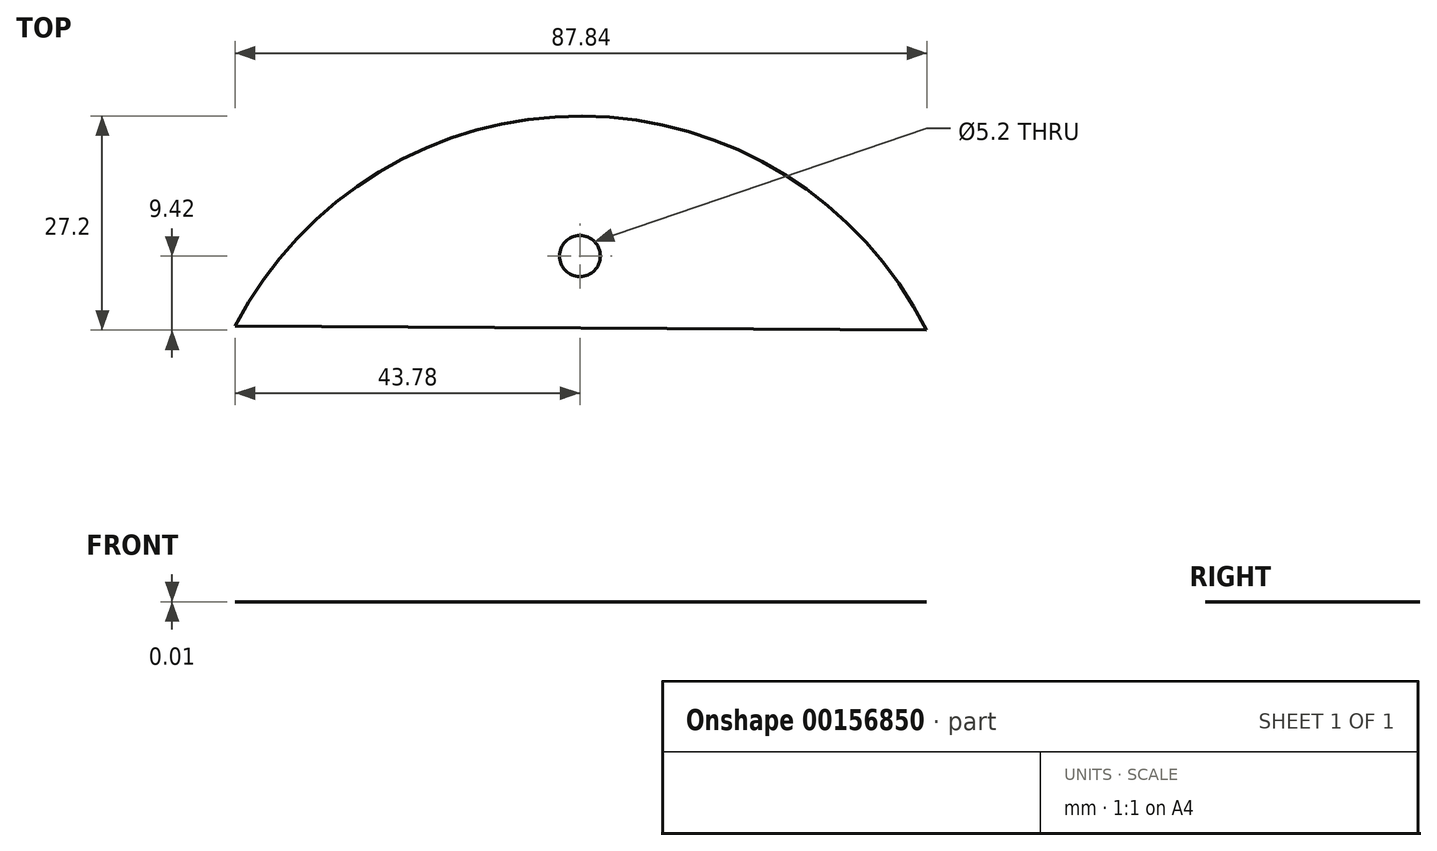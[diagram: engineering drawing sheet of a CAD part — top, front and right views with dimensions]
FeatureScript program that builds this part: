
annotation { "Feature Type Name" : "Feature", "Feature Type Description" : "" }
export const myFeature = defineFeature(function(context is Context, id is Id, definition is map)
    precondition{}
    {
        {
            var Q0;
            Q0=qCreatedBy(makeId("Top.planeOp"),FACE);
            var sketch = newSketch(context, id + "F0", { "sketchPlane" : qUnion([Q0])});
            skPoint(sketch, "E0.center.orphan", {"position": v(0, 0) * mm});
            skPoint(sketch, "E0.end.orphan", {"position": v(43.38, -20.08) * mm});
            skPoint(sketch, "E0.start.orphan", {"position": v(-43.12, -20.62) * mm});
            skArc(sketch, "E1", {"start": v(44.06, 22.08) * mm, "mid": v(0.3, 49.28) * mm, "end": v(-43.78, 22.62) * mm});
            skPoint(sketch, "E2.orphan", {"position": v(-43.12, 20.62) * mm});
            skPoint(sketch, "E3.orphan", {"position": v(43.38, 20.08) * mm});
            skCircle(sketch, "E4", {"center": v(0, 31.5) * mm, "radius": 2.6 * mm});
            skLineSegment(sketch, "E5.0", {"start": v(-43.78, 22.62) * mm, "end": v(44.06, 22.08) * mm});
            skPoint(sketch, "E6.orphan", {"position": v(-44.75, 20.63) * mm});
            skPoint(sketch, "E7.orphan", {"position": v(45, 20.07) * mm});
            skSolve(sketch);
        }
        {
            var Q0;
            Q0 = qSketchRegion(id + "F0", true);
            extrude(context, id + "F1", {"entities" : qUnion([Q0]), "depth" : 1 / 101.6 * mm});
        }
    });
